# Revit family: CW75
name_source: partatom
category: Generic Models
revit_build: Autodesk Revit LT 2017 (Build: 20160225_1515(x64)
units: mm (PartAtom-declared; Revit-internal decimal feet)

## family parameters
Always vertical = No
Can host rebar = No
Cut with Voids When Loaded = No
Part Type = Normal
Room Calculation Point = No
Round Connector Dimension = Use Diameter
Shared = No
Work Plane-Based = Yes

## types (1)
- NBS Standard Parameters
    BIMObjectName = Metpro_metprolibrary_cablegland_brass_external
    Default Elevation = 1219 mm
    Description = CW75 - 75mm Cable Gland Kit
    DurationUnit = year
    Finish = Self Colour
    Keynote = Kit Comprises of 1 Gland C/W Seal, 1 Shroud, 1 Tag and 1 Locknut
    ManufacturerName = Metpro Ltd
    ManufacturerURL = www.metpro.co.uk
    Material = Brass
    ModelReference = CW75
    NBSDescription = High Voltage Cable Glands
    NominalHeight = 70 mm  [stored 0.229659 ft]
    NominalLength = 95 mm
    NominalWidth = 95 mm
    ProductInformation = www.metpro.co.uk/pdf/cw75.pdf
    Size = 75mm
    Uniclass2 = Pr_65_70_36_33
    Version = 1
    WarrantyDurationUnit = 1 year
    Weight = 2.15Kg

note: [stored X ft] marks values corroborated as IEEE doubles in the binary element streams (Revit-internal decimal feet)

## geometry (parser evidence)
native form markers: Sweep x2
no freeform markers — native parametric forms only
